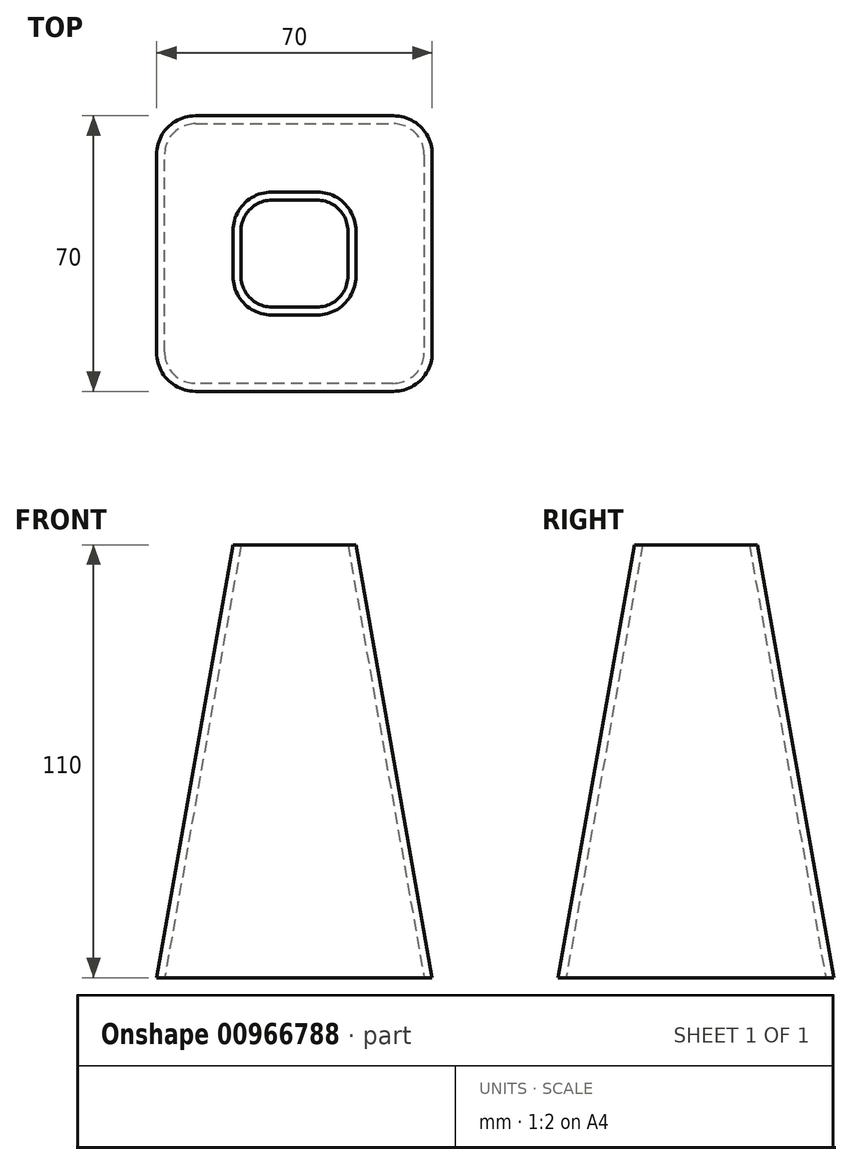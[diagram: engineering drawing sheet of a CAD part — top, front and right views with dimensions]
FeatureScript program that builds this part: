
annotation { "Feature Type Name" : "Feature", "Feature Type Description" : "" }
export const myFeature = defineFeature(function(context is Context, id is Id, definition is map)
    precondition{}
    {
        {
            var Q0;
            Q0=qCreatedBy(makeId("Top.planeOp"),FACE);
            var sketch = newSketch(context, id + "F0", { "sketchPlane" : qUnion([Q0])});
            skLineSegment(sketch, "E0.bottom", {"start": v(35, -35) * mm, "end": v(-35, -35) * mm});
            skLineSegment(sketch, "E0.top", {"start": v(35, 35) * mm, "end": v(-35, 35) * mm});
            skLineSegment(sketch, "E0.left", {"start": v(35, -35) * mm, "end": v(35, 35) * mm});
            skLineSegment(sketch, "E0.right", {"start": v(-35, -35) * mm, "end": v(-35, 35) * mm});
            skPoint(sketch, "E0.middle", {"position": v(0, 0) * mm});
            skSolve(sketch);
        }
        {
            var Q0;
            Q0=makeQuery(id+"F0.imprint","IMPRINT",FACE,{"disambiguationData":[TD([[makeQuery(id+"F0.imprint","IMPRINT",EDGE,{"derivedFrom":sQuery(id+"F0.wireOp",EDGE,"E0.bottom")}),-1.0]])]});
            extrude(context, id + "F1", {"entities" : qUnion([Q0]), "depth" : 110 * mm, "offsetDistance" : 25 * mm, "hasDraft" : true, "draftAngle" : 10 * degree, "draftPullDirection" : true});
        }
        {
            var Q0;
            Q0=makeQuery(id+"F1.opExtrude","SWEPT_EDGE",EDGE,{"disambiguationData":[OSD([sQuery(id+"F0.wireOp",EDGE,"E0.bottom"),sQuery(id+"F0.wireOp",EDGE,"E0.left")])]});
            var Q1;
            Q1=makeQuery(id+"F1.opExtrude","SWEPT_EDGE",EDGE,{"disambiguationData":[OSD([sQuery(id+"F0.wireOp",EDGE,"E0.top"),sQuery(id+"F0.wireOp",EDGE,"E0.left")])]});
            var Q2;
            Q2=makeQuery(id+"F1.opExtrude","SWEPT_EDGE",EDGE,{"disambiguationData":[OSD([sQuery(id+"F0.wireOp",EDGE,"E0.bottom"),sQuery(id+"F0.wireOp",EDGE,"E0.right")])]});
            var Q3;
            Q3=makeQuery(id+"F1.opExtrude","SWEPT_EDGE",EDGE,{"disambiguationData":[OSD([sQuery(id+"F0.wireOp",EDGE,"E0.top"),sQuery(id+"F0.wireOp",EDGE,"E0.right")])]});
            fillet(context, id + "F2", {"entities" : qUnion([Q0, Q1, Q2, Q3]), "radius" : 10 * mm, "tangentPropagation" : true, "allowEdgeOverflow" : false});
        }
        {
            var Q0;
            Q0=makeQuery(id+"F1.opExtrude","CAP_FACE",FACE,{"disambiguationData":[OSD([sQuery(id+"F0.wireOp",EDGE,"E0.bottom"),sQuery(id+"F0.wireOp",EDGE,"E0.top"),sQuery(id+"F0.wireOp",EDGE,"E0.left"),sQuery(id+"F0.wireOp",EDGE,"E0.right")])],"isStart":true});
            var Q1;
            Q1=makeQuery(id+"F1.opExtrude","CAP_FACE",FACE,{"disambiguationData":[OSD([sQuery(id+"F0.wireOp",EDGE,"E0.bottom"),sQuery(id+"F0.wireOp",EDGE,"E0.top"),sQuery(id+"F0.wireOp",EDGE,"E0.left"),sQuery(id+"F0.wireOp",EDGE,"E0.right")])],"isStart":false});
            shell(context, id + "F3", {"entities" : qUnion([Q0, Q1]), "thickness" : 2 * mm});
        }
    });
